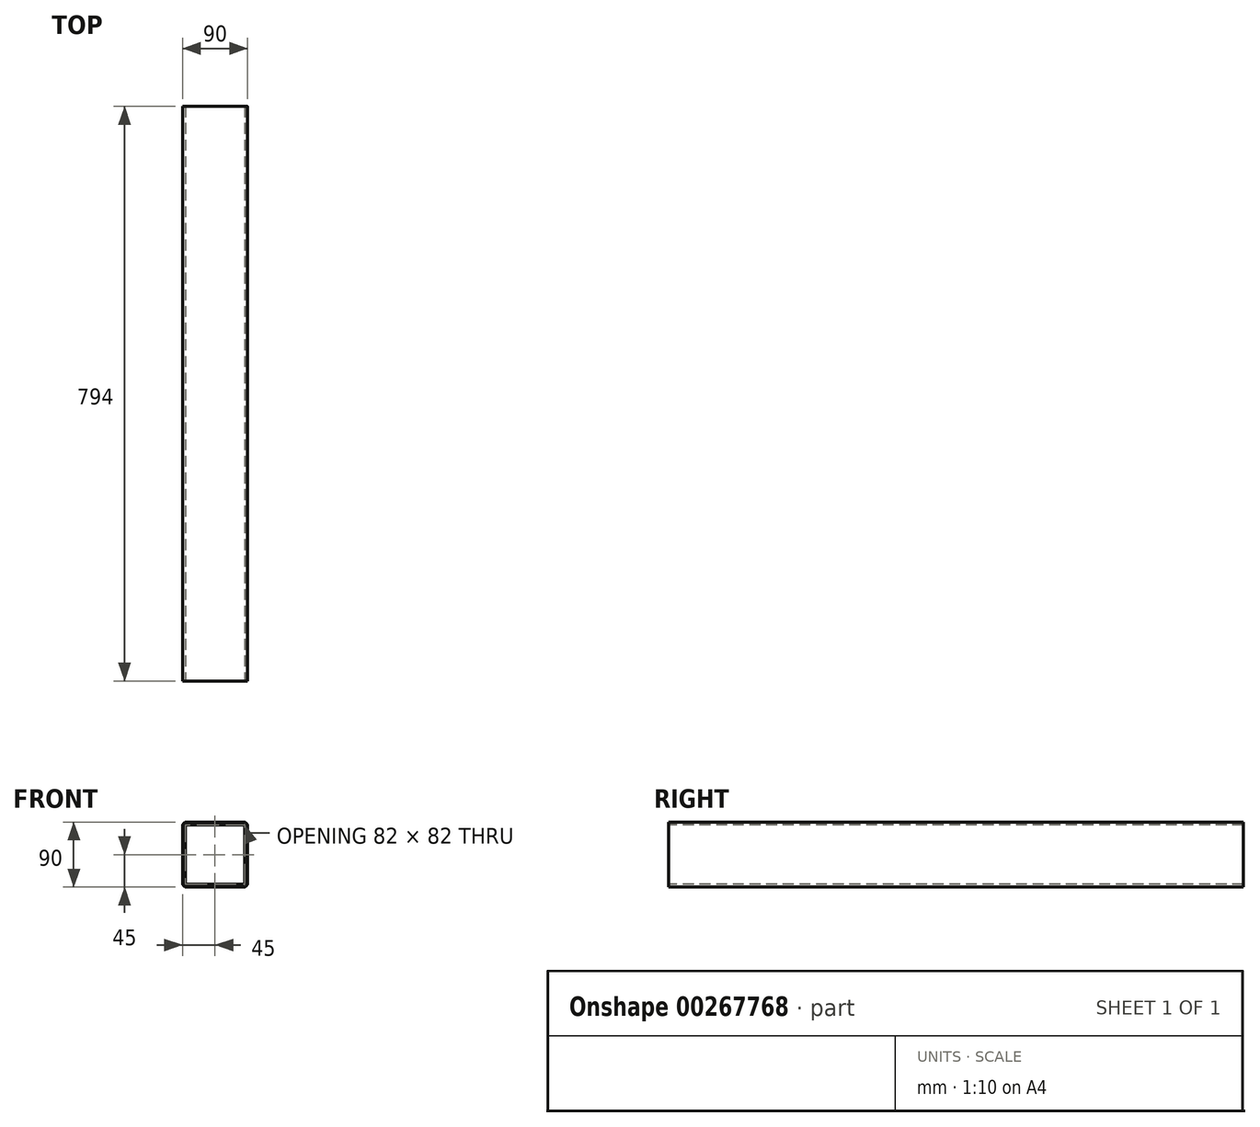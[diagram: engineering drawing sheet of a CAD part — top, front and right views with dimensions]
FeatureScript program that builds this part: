
annotation { "Feature Type Name" : "Feature", "Feature Type Description" : "" }
export const myFeature = defineFeature(function(context is Context, id is Id, definition is map)
    precondition{}
    {
        {
            var Q0;
            Q0=qCreatedBy(makeId("Front.planeOp"),FACE);
            var sketch = newSketch(context, id + "F0", { "sketchPlane" : qUnion([Q0])});
            skLineSegment(sketch, "E0.bottom", {"start": v(39, 45) * mm, "end": v(-39, 45) * mm});
            skLineSegment(sketch, "E0.top", {"start": v(39, -45) * mm, "end": v(-39, -45) * mm});
            skLineSegment(sketch, "E0.left", {"start": v(45, 39) * mm, "end": v(45, -39) * mm});
            skLineSegment(sketch, "E0.right", {"start": v(-45, 39) * mm, "end": v(-45, -39) * mm});
            skPoint(sketch, "E0.middle", {"position": v(0, 0) * mm});
            skPoint(sketch, "E1.visualSharp", {"position": v(-45, 45) * mm});
            skArc(sketch, "E1.filletArc", {"start": v(-39, 45) * mm, "mid": v(-43.24, 43.24) * mm, "end": v(-45, 39) * mm});
            skPoint(sketch, "E2.visualSharp", {"position": v(45, 45) * mm});
            skArc(sketch, "E2.filletArc", {"start": v(45, 39) * mm, "mid": v(43.24, 43.24) * mm, "end": v(39, 45) * mm});
            skPoint(sketch, "E3.visualSharp", {"position": v(45, -45) * mm});
            skArc(sketch, "E3.filletArc", {"start": v(39, -45) * mm, "mid": v(43.24, -43.24) * mm, "end": v(45, -39) * mm});
            skPoint(sketch, "E4.visualSharp", {"position": v(-45, -45) * mm});
            skArc(sketch, "E4.filletArc", {"start": v(-45, -39) * mm, "mid": v(-43.24, -43.24) * mm, "end": v(-39, -45) * mm});
            skArc(sketch, "E5.0", {"start": v(-39, 41) * mm, "mid": v(-40.41, 40.41) * mm, "end": v(-41, 39) * mm});
            skLineSegment(sketch, "E5.1", {"start": v(39, 41) * mm, "end": v(-39, 41) * mm});
            skLineSegment(sketch, "E5.2", {"start": v(-41, 39) * mm, "end": v(-41, -39) * mm});
            skArc(sketch, "E5.3", {"start": v(41, 39) * mm, "mid": v(40.41, 40.41) * mm, "end": v(39, 41) * mm});
            skArc(sketch, "E5.4", {"start": v(-41, -39) * mm, "mid": v(-40.41, -40.41) * mm, "end": v(-39, -41) * mm});
            skLineSegment(sketch, "E5.5", {"start": v(39, -41) * mm, "end": v(-39, -41) * mm});
            skArc(sketch, "E5.6", {"start": v(39, -41) * mm, "mid": v(40.41, -40.41) * mm, "end": v(41, -39) * mm});
            skLineSegment(sketch, "E5.7", {"start": v(41, 39) * mm, "end": v(41, -39) * mm});
            skSolve(sketch);
        }
        {
            var Q0;
            Q0=makeQuery(id+"F0.imprint","IMPRINT",FACE,{"disambiguationData":[TD([[makeQuery(id+"F0.imprint","IMPRINT",EDGE,{"derivedFrom":sQuery(id+"F0.wireOp",EDGE,"E0.bottom")}),1.0]])]});
            extrude(context, id + "F1", {"entities" : qUnion([Q0]), "oppositeDirection" : true, "depth" : 794 * mm});
        }
    });
